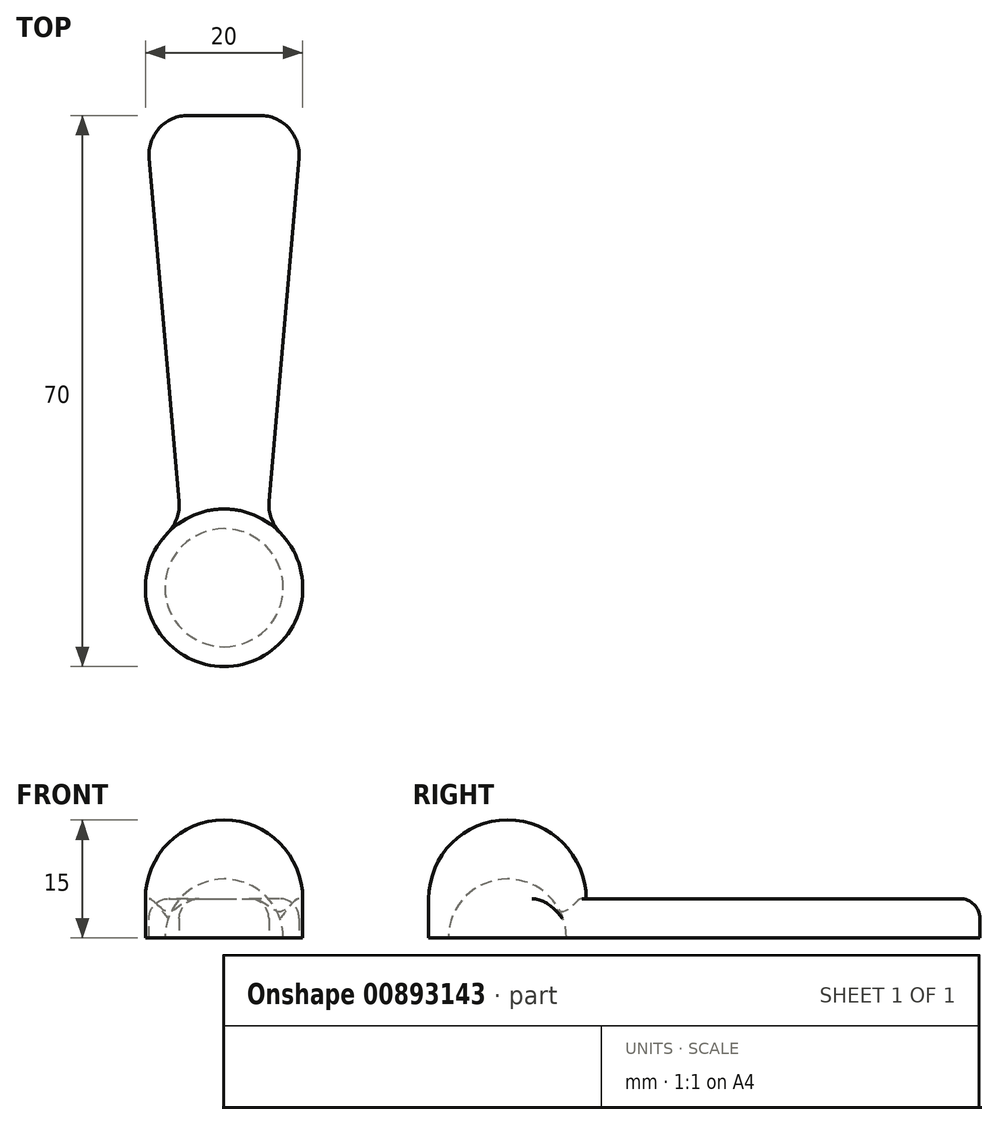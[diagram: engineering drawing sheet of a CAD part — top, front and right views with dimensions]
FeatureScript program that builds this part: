
annotation { "Feature Type Name" : "Feature", "Feature Type Description" : "" }
export const myFeature = defineFeature(function(context is Context, id is Id, definition is map)
    precondition{}
    {
        {
            var Q0;
            Q0=qCreatedBy(makeId("Top.planeOp"),FACE);
            var sketch = newSketch(context, id + "F0", { "sketchPlane" : qUnion([Q0])});
            skCircle(sketch, "E0", {"center": v(0, 0) * mm, "radius": 10 * mm});
            skLineSegment(sketch, "E1", {"start": v(0, 60) * mm, "end": v(0, 0) * mm, "construction": true});
            skLineSegment(sketch, "E2", {"start": v(0, 60) * mm, "end": v(-10, 60) * mm});
            skLineSegment(sketch, "E3", {"start": v(-10, 60) * mm, "end": v(-5.48, 8.36) * mm});
            skLineSegment(sketch, "E4.MirrorCS", {"start": v(0, 60) * mm, "end": v(10, 60) * mm});
            skLineSegment(sketch, "E5.MirrorCS", {"start": v(10, 60) * mm, "end": v(5.48, 8.36) * mm});
            skSolve(sketch);
        }
        {
            var Q0;
            {var subQ0=sQuery(id+"F0.wireOp",EDGE,"E0");var subQ1=makeQuery(id+"F0.imprint","INTERSECT",VERTEX,{"derivedFrom":[subQ0,sQuery(id+"F0.wireOp",EDGE,"E3")]});Q0=makeQuery(id+"F0.imprint","IMPRINT",FACE,{"disambiguationData":[TD([[makeQuery(id+"F0.imprint","IMPRINT",EDGE,{"disambiguationData":[TD([[subQ1,1.0]])],"derivedFrom":subQ0}),1.0]])]});}
            var Q1;
            Q1=makeQuery(id+"F0.imprint","IMPRINT",FACE,{"disambiguationData":[TD([[makeQuery(id+"F0.imprint","IMPRINT",EDGE,{"derivedFrom":sQuery(id+"F0.wireOp",EDGE,"E2")}),1.0]])]});
            extrude(context, id + "F1", {"entities" : qUnion([Q0, Q1]), "depth" : 5 * mm, "offsetDistance" : 25 * mm});
        }
        {
            var Q0;
            Q0=makeQuery(id+"F1.opExtrude","CAP_FACE",FACE,{"disambiguationData":[OSD([sQuery(id+"F0.wireOp",EDGE,"E0"),sQuery(id+"F0.wireOp",EDGE,"E2"),sQuery(id+"F0.wireOp",EDGE,"E3"),sQuery(id+"F0.wireOp",EDGE,"E4.MirrorCS"),sQuery(id+"F0.wireOp",EDGE,"E5.MirrorCS")])],"isStart":false});
            var sketch = newSketch(context, id + "F2", { "sketchPlane" : qUnion([Q0])});
            skArc(sketch, "E6", {"start": v(0, 10) * mm, "mid": v(-10, 0) * mm, "end": v(0, -10) * mm});
            skLineSegment(sketch, "E7", {"start": v(0, -10) * mm, "end": v(0, 10) * mm});
            skSolve(sketch);
        }
        {
            var Q0;
            {var subQ2=sQuery(id+"F2.wireOp",EDGE,"E7");Q0=makeQuery(id+"F2.imprint","IMPRINT",FACE,{"disambiguationData":[TD([[makeQuery(id+"F2.imprint","IMPRINT",EDGE,{"derivedFrom":subQ2}),1.0]])]});}
            var Q1;
            Q1=sQuery(id+"F2.wireOp",EDGE,"E7");
            revolve(context, id + "F3", {"operationType" : NewBodyOperationType.ADD, "surfaceOperationType" : NewSurfaceOperationType.NEW, "entities" : qUnion([Q0]), "axis" : qUnion([Q1]), "revolveType" : RevolveType.ONE_DIRECTION, "angle" : 180 * degree});
        }
        {
            var Q0;
            Q0=makeQuery(id+"F1.opExtrude","CAP_FACE",FACE,{"disambiguationData":[OSD([sQuery(id+"F0.wireOp",EDGE,"E0"),sQuery(id+"F0.wireOp",EDGE,"E2"),sQuery(id+"F0.wireOp",EDGE,"E3"),sQuery(id+"F0.wireOp",EDGE,"E4.MirrorCS"),sQuery(id+"F0.wireOp",EDGE,"E5.MirrorCS")])],"isStart":true});
            var sketch = newSketch(context, id + "F4", { "sketchPlane" : qUnion([Q0])});
            skCircle(sketch, "E8", {"center": v(0, 0) * mm, "radius": 7.5 * mm});
            skLineSegment(sketch, "E9", {"start": v(0, 7.5) * mm, "end": v(0, -7.5) * mm});
            skSolve(sketch);
        }
        {
            var Q0;
            {var subQ0=sQuery(id+"F4.wireOp",EDGE,"E9");Q0=makeQuery(id+"F4.imprint","IMPRINT",FACE,{"disambiguationData":[TD([[makeQuery(id+"F4.imprint","IMPRINT",EDGE,{"derivedFrom":subQ0}),-1.0]])]});}
            var Q1;
            Q1=sQuery(id+"F4.wireOp",EDGE,"E9");
            revolve(context, id + "F5", {"operationType" : NewBodyOperationType.REMOVE, "surfaceOperationType" : NewSurfaceOperationType.NEW, "entities" : qUnion([Q0]), "axis" : qUnion([Q1]), "revolveType" : RevolveType.FULL, "oppositeDirection" : true});
        }
        {
            var Q0;
            Q0=makeQuery(id+"F1.opExtrude","SWEPT_EDGE",EDGE,{"disambiguationData":[OSD([sQuery(id+"F0.wireOp",EDGE,"E2"),sQuery(id+"F0.wireOp",EDGE,"E3")])]});
            var Q1;
            Q1=makeQuery(id+"F1.opExtrude","SWEPT_EDGE",EDGE,{"disambiguationData":[OSD([sQuery(id+"F0.wireOp",EDGE,"E4.MirrorCS"),sQuery(id+"F0.wireOp",EDGE,"E5.MirrorCS")])]});
            var Q2;
            Q2=makeQuery(id+"F1.opExtrude","SWEPT_EDGE",EDGE,{"disambiguationData":[OSD([sQuery(id+"F0.wireOp",EDGE,"E0"),sQuery(id+"F0.wireOp",EDGE,"E5.MirrorCS")])]});
            var Q3;
            Q3=makeQuery(id+"F1.opExtrude","SWEPT_EDGE",EDGE,{"disambiguationData":[OSD([sQuery(id+"F0.wireOp",EDGE,"E0"),sQuery(id+"F0.wireOp",EDGE,"E3")])]});
            fillet(context, id + "F6", {"entities" : qUnion([Q0, Q1, Q2, Q3]), "radius" : 5 * mm, "tangentPropagation" : true, "allowEdgeOverflow" : false});
        }
        {
            var Q0;
            Q0=makeQuery(id+"F1.opExtrude","CAP_EDGE",EDGE,{"disambiguationData":[OSD([sQuery(id+"F0.wireOp",EDGE,"E3")])],"isStart":false});
            fillet(context, id + "F7", {"entities" : qUnion([Q0]), "radius" : 2.5 * mm, "tangentPropagation" : true, "allowEdgeOverflow" : false});
        }
    });
